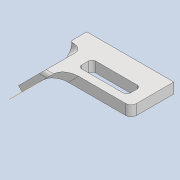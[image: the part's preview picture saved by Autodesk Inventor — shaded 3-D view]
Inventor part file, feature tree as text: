
AUTODESK INVENTOR PART (.ipt)
format: ipt  version: 2020 (Build 240168000, 168)  size: 230,912 bytes
history: native  units: mm
features: fillet x8, sketch x6, extrude x6, other x5, projected_geometry x4, reference x3, plane x2, chamfer x1, thicken_offset x1
ambient origin geometry x8: Origin, YZ Plane, XZ Plane, XY Plane, X Axis, Y Axis, Z Axis, Center Point
bodies: Solid1 (feature_tree)
feature tree (36):
  sketch  "Sketch1"  dims[d0=10.0mm d1=0.0mm d2=18.0mm d3=0.0mm]
  plane  "Work Plane1"
  extrude  "Extrusion1"  Depth=10.0mm TaperAngle=0.0deg
  extrude  "Extrusion2"  Depth=2.0mm
  plane  "Work Plane2"
  extrude  "Extrusion3"  Depth=20.0mm
  extrude  "Extrusion4"  Depth=3.0mm TaperAngle=0.0deg
  extrude  "Extrusion5"  Depth=3.0mm TaperAngle=0.0deg
  extrude  "Extrusion6"  Depth=8.0mm
  fillet  "Fillet1"  Radius=15.0mm
  fillet  "Fillet2"  Radius=2.0mm
  fillet  "Fillet3"  Radius=6.0mm
  fillet  "Fillet4"  Radius=2.0mm
  fillet  "Fillet5"  Radius=4.0mm
  fillet  "Fillet6"  Radius=1.0mm
  fillet  "Fillet7"  Radius=3.0mm
  chamfer  "Chamfer1"  Distance=3.0mm
  thicken_offset  "Thicken1"
  fillet  "Fillet8"  Radius=2.0mm
  reference  "Reference1"
  sketch  "Sketch2"  dims[d4=2.0mm d5=2.0mm]
  projected_geometry  "Projected Loop1"
  sketch  "Sketch3"  dims[d6=5.0mm d7=20.0mm]
  reference  "Reference2"
  sketch  "Sketch4"  dims[d8=8.0mm d9=3.0mm d10=0.0mm]
  projected_geometry  "Projected Loop2"
  sketch  "Sketch5"  dims[d11=3.0mm d12=0.0mm d13=15.0mm d14=0.0mm]
  projected_geometry  "Projected Loop3"
  sketch  "Sketch6"  dims[d15=20.0mm d16=8.0mm d17=15.0mm d18=0.0mm d19=2.0mm d20=6.0mm d21=2.0mm d22=4.0mm d23=1.0mm d24=3.0mm d25=3.0mm d26=2.0mm d27=2.0mm d28=45.0deg d29=8.0mm d30=8.0mm d31=3.0mm]
  reference  "Reference3"
  projected_geometry  "Projected Loop4"
  parser-record x1  (decoder bookkeeping rows leaked as tree rows — omitted from the tree; the rows remain in map.json)
  other  "driver_unit_1.iam"
  other  "drv_stand_1:1"
  other  "mot_holder_1:1"
  other  "tendon_wh_3:1"
note: 1 file-system path scrubbed to <path> (originals preserved in map.json)
